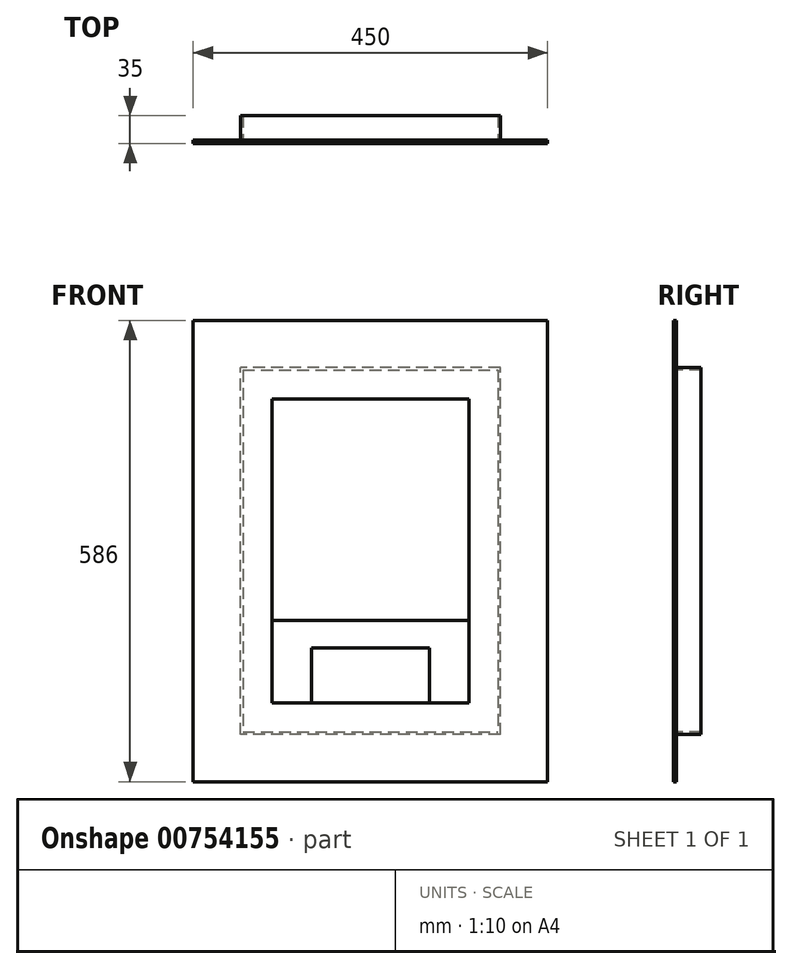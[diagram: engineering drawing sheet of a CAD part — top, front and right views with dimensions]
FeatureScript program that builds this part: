
annotation { "Feature Type Name" : "Feature", "Feature Type Description" : "" }
export const myFeature = defineFeature(function(context is Context, id is Id, definition is map)
    precondition{}
    {
        {
            var Q0;
            Q0=qCreatedBy(makeId("Front.planeOp"),FACE);
            var sketch = newSketch(context, id + "F0", { "sketchPlane" : qUnion([Q0])});
            skLineSegment(sketch, "E0.bottom", {"start": v(-219.76, 309.54) * mm, "end": v(230.24, 309.54) * mm});
            skLineSegment(sketch, "E0.top", {"start": v(-219.76, -276.46) * mm, "end": v(230.24, -276.46) * mm});
            skLineSegment(sketch, "E0.left", {"start": v(-219.76, 309.54) * mm, "end": v(-219.76, -276.46) * mm});
            skLineSegment(sketch, "E0.right", {"start": v(230.24, 309.54) * mm, "end": v(230.24, -276.46) * mm});
            skLineSegment(sketch, "E1.bottom", {"start": v(-119.76, 209.54) * mm, "end": v(130.24, 209.54) * mm});
            skLineSegment(sketch, "E1.top", {"start": v(-119.76, -176.46) * mm, "end": v(130.24, -176.46) * mm});
            skLineSegment(sketch, "E1.left", {"start": v(-119.76, 209.54) * mm, "end": v(-119.76, -176.46) * mm});
            skLineSegment(sketch, "E1.right", {"start": v(130.24, 209.54) * mm, "end": v(130.24, -176.46) * mm});
            skSolve(sketch);
        }
        {
            var Q0;
            Q0=makeQuery(id+"F0.imprint","IMPRINT",FACE,{"disambiguationData":[TD([[makeQuery(id+"F0.imprint","IMPRINT",EDGE,{"derivedFrom":sQuery(id+"F0.wireOp",EDGE,"E0.bottom")}),-1.0]])]});
            extrude(context, id + "F1", {"entities" : qUnion([Q0]), "depth" : 4 * mm, "offsetDistance" : 25 * mm});
        }
        {
            var Q0;
            Q0=qCreatedBy(makeId("Front.planeOp"),FACE);
            var sketch = newSketch(context, id + "F2", { "sketchPlane" : qUnion([Q0])});
            skLineSegment(sketch, "E2.bottom", {"start": v(-119.76, 209.54) * mm, "end": v(130.24, 209.54) * mm});
            skLineSegment(sketch, "E2.top", {"start": v(-119.76, -71.46) * mm, "end": v(130.24, -71.46) * mm});
            skLineSegment(sketch, "E2.left", {"start": v(-119.76, 209.54) * mm, "end": v(-119.76, -71.46) * mm});
            skLineSegment(sketch, "E2.right", {"start": v(130.24, 209.54) * mm, "end": v(130.24, -71.46) * mm});
            skLineSegment(sketch, "E3", {"start": v(5.24, 209.54) * mm, "end": v(5.24, -189.61) * mm, "construction": true});
            skLineSegment(sketch, "E4.bottom", {"start": v(-69.76, -106.46) * mm, "end": v(80.24, -106.46) * mm});
            skLineSegment(sketch, "E4.top", {"start": v(-69.76, -176.46) * mm, "end": v(80.24, -176.46) * mm});
            skLineSegment(sketch, "E4.left", {"start": v(-69.76, -106.46) * mm, "end": v(-69.76, -176.46) * mm});
            skLineSegment(sketch, "E4.right", {"start": v(80.24, -106.46) * mm, "end": v(80.24, -176.46) * mm});
            skLineSegment(sketch, "E5.bottom", {"start": v(-159.76, 249.54) * mm, "end": v(170.24, 249.54) * mm});
            skLineSegment(sketch, "E5.top", {"start": v(-159.76, -216.46) * mm, "end": v(170.24, -216.46) * mm});
            skLineSegment(sketch, "E5.left", {"start": v(-159.76, 249.54) * mm, "end": v(-159.76, -216.46) * mm});
            skLineSegment(sketch, "E5.right", {"start": v(170.24, 249.54) * mm, "end": v(170.24, -216.46) * mm});
            skSolve(sketch);
        }
        {
            var Q0;
            Q0=makeQuery(id+"F2.imprint","IMPRINT",FACE,{"disambiguationData":[TD([[makeQuery(id+"F2.imprint","IMPRINT",EDGE,{"derivedFrom":sQuery(id+"F2.wireOp",EDGE,"E2.bottom")}),1.0]])]});
            extrude(context, id + "F3", {"entities" : qUnion([Q0]), "depth" : 3 * mm, "offsetDistance" : 25 * mm});
        }
        {
            var Q0;
            Q0=makeQuery(id+"F3.opExtrude","CAP_FACE",FACE,{"disambiguationData":[OSD([sQuery(id+"F2.wireOp",EDGE,"E2.bottom"),sQuery(id+"F2.wireOp",EDGE,"E2.top"),sQuery(id+"F2.wireOp",EDGE,"E2.left"),sQuery(id+"F2.wireOp",EDGE,"E2.right"),sQuery(id+"F2.wireOp",EDGE,"E4.bottom"),sQuery(id+"F2.wireOp",EDGE,"E4.top"),sQuery(id+"F2.wireOp",EDGE,"E4.left"),sQuery(id+"F2.wireOp",EDGE,"E4.right"),sQuery(id+"F2.wireOp",EDGE,"E5.bottom"),sQuery(id+"F2.wireOp",EDGE,"E5.top"),sQuery(id+"F2.wireOp",EDGE,"E5.left"),sQuery(id+"F2.wireOp",EDGE,"E5.right")])],"isStart":true});
            var sketch = newSketch(context, id + "F4", { "sketchPlane" : qUnion([Q0])});
            skLineSegment(sketch, "E6.0", {"start": v(156.76, 246.54) * mm, "end": v(-167.24, 246.54) * mm});
            skLineSegment(sketch, "E6.1", {"start": v(156.76, 246.54) * mm, "end": v(156.76, -213.46) * mm});
            skLineSegment(sketch, "E6.2", {"start": v(156.76, -213.46) * mm, "end": v(-167.24, -213.46) * mm});
            skLineSegment(sketch, "E6.3", {"start": v(-167.24, 246.54) * mm, "end": v(-167.24, -213.46) * mm});
            skSolve(sketch);
        }
        {
            var Q0;
            Q0=makeQuery(id+"F4.imprint","IMPRINT",FACE,{"disambiguationData":[TD([[makeQuery(id+"F4.imprint","IMPRINT",EDGE,{"derivedFrom":sQuery(id+"F4.wireOp",EDGE,"E6.0")}),-1.0]])]});
            extrude(context, id + "F5", {"entities" : qUnion([Q0]), "operationType" : NewBodyOperationType.ADD, "depth" : 31 * mm, "offsetDistance" : 25 * mm});
        }
    });
